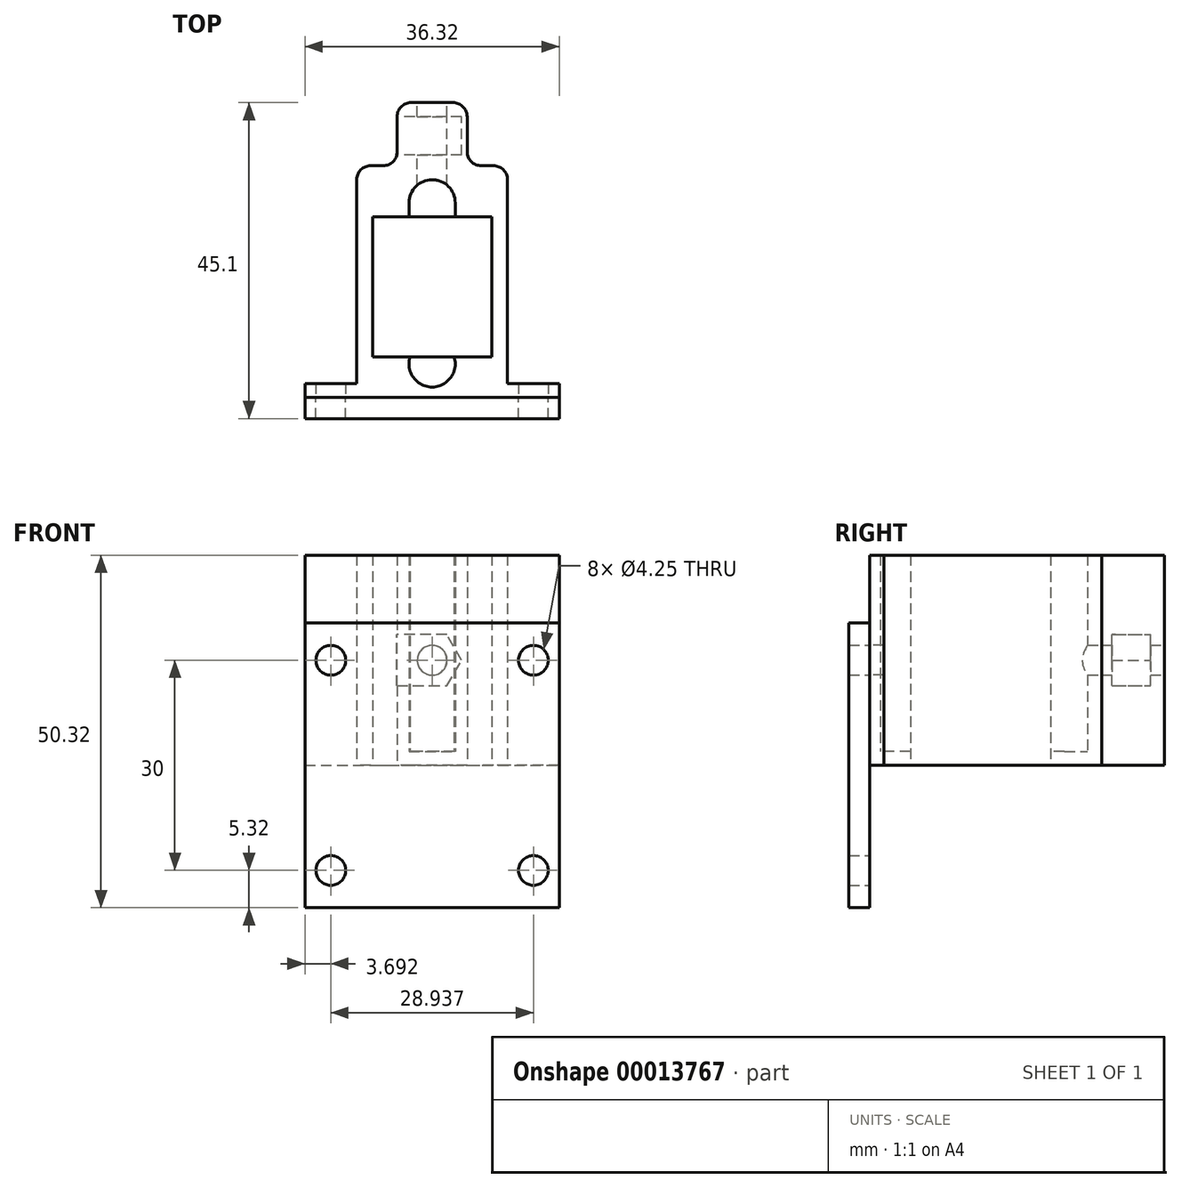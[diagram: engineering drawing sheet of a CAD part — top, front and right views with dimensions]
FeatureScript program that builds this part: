
annotation { "Feature Type Name" : "Feature", "Feature Type Description" : "" }
export const myFeature = defineFeature(function(context is Context, id is Id, definition is map)
    precondition{}
    {
        {
            var Q0;
            Q0=qCreatedBy(makeId("Top.planeOp"),FACE);
            var sketch = newSketch(context, id + "F0", { "sketchPlane" : qUnion([Q0])});
            skLineSegment(sketch, "E0.rect.bottom", {"start": v(8.5, -10) * mm, "end": v(-8.5, -10) * mm, "construction": true});
            skLineSegment(sketch, "E0.rect.top", {"start": v(8.5, 10) * mm, "end": v(-8.5, 10) * mm, "construction": true});
            skLineSegment(sketch, "E0.rect.left", {"start": v(8.5, -10) * mm, "end": v(8.5, 10) * mm, "construction": true});
            skLineSegment(sketch, "E0.rect.right", {"start": v(-8.5, -10) * mm, "end": v(-8.5, 10) * mm, "construction": true});
            skPoint(sketch, "E0.rect.middle", {"position": v(0, 0) * mm});
            skArc(sketch, "E1", {"start": v(3.3, 12) * mm, "mid": v(0, 15.3) * mm, "end": v(-3.3, 12) * mm});
            skArc(sketch, "E2", {"start": v(-3.14, -10) * mm, "mid": v(0, -14.3) * mm, "end": v(3.14, -10) * mm});
            skLineSegment(sketch, "E3", {"start": v(-3.3, 10) * mm, "end": v(-3.3, 12) * mm});
            skLineSegment(sketch, "E4", {"start": v(3.3, 10) * mm, "end": v(3.3, 12) * mm});
            skLineSegment(sketch, "E5", {"start": v(-3.3, 10) * mm, "end": v(-8.5, 10) * mm});
            skLineSegment(sketch, "E6", {"start": v(-8.5, -10) * mm, "end": v(-3.14, -10) * mm});
            skLineSegment(sketch, "E7", {"start": v(-8.5, 10) * mm, "end": v(-8.5, -10) * mm});
            skLineSegment(sketch, "E8.0.MirrorCS", {"start": v(3.3, 10) * mm, "end": v(8.5, 10) * mm});
            skLineSegment(sketch, "E9.0.MirrorCS", {"start": v(8.5, 10) * mm, "end": v(8.5, -10) * mm});
            skLineSegment(sketch, "E10.0.MirrorCS", {"start": v(8.5, -10) * mm, "end": v(3.14, -10) * mm});
            skPoint(sketch, "E11.center.orphan", {"position": v(0, 10) * mm});
            skLineSegment(sketch, "E12", {"start": v(0, -15.8) * mm, "end": v(-10.77, -15.8) * mm});
            skLineSegment(sketch, "E13", {"start": v(-10.77, -15.8) * mm, "end": v(-10.77, 17.3) * mm});
            skLineSegment(sketch, "E14", {"start": v(-10.77, 17.3) * mm, "end": v(-5, 17.3) * mm});
            skLineSegment(sketch, "E15.0.MirrorCS", {"start": v(10.77, 17.3) * mm, "end": v(5, 17.3) * mm});
            skLineSegment(sketch, "E16.0.MirrorCS", {"start": v(10.77, -15.8) * mm, "end": v(10.77, 17.3) * mm});
            skLineSegment(sketch, "E17.0.MirrorCS", {"start": v(0, -15.8) * mm, "end": v(10.77, -15.8) * mm});
            skLineSegment(sketch, "E18", {"start": v(-5, 17.3) * mm, "end": v(-5, 26.3) * mm});
            skLineSegment(sketch, "E19", {"start": v(-5, 26.3) * mm, "end": v(0, 26.3) * mm});
            skLineSegment(sketch, "E20.0.MirrorCS", {"start": v(5, 17.3) * mm, "end": v(5, 26.3) * mm});
            skLineSegment(sketch, "E21.0.MirrorCS", {"start": v(5, 26.3) * mm, "end": v(0, 26.3) * mm});
            skPoint(sketch, "E22.orphan", {"position": v(0, 17.3) * mm});
            skSolve(sketch);
        }
        {
            var Q0;
            Q0 = qSketchRegion(id + "F0", true);
            var Q1;
            Q1=makeQuery(id+"F0.imprint","IMPRINT",FACE,{"disambiguationData":[TD([[makeQuery(id+"F0.imprint","IMPRINT",EDGE,{"derivedFrom":sQuery(id+"F0.wireOp",EDGE,"E1")}),1.0]])]});
            extrude(context, id + "F1", {"entities" : qUnion([Q0, Q1]), "depth" : 2 * mm});
        }
        {
            var Q0;
            Q0 = qSketchRegion(id + "F0", true);
            extrude(context, id + "F2", {"entities" : qUnion([Q0]), "operationType" : NewBodyOperationType.ADD, "depth" : 30 * mm});
        }
        {
            var Q0;
            Q0=makeQuery(id+"F1.opExtrude","CAP_FACE",FACE,{"disambiguationData":[OSD([sQuery(id+"F0.wireOp",EDGE,"E12"),sQuery(id+"F0.wireOp",EDGE,"E13"),sQuery(id+"F0.wireOp",EDGE,"E14"),sQuery(id+"F0.wireOp",EDGE,"E15.0.MirrorCS"),sQuery(id+"F0.wireOp",EDGE,"E16.0.MirrorCS"),sQuery(id+"F0.wireOp",EDGE,"E17.0.MirrorCS"),sQuery(id+"F0.wireOp",EDGE,"E18"),sQuery(id+"F0.wireOp",EDGE,"E19"),sQuery(id+"F0.wireOp",EDGE,"E20.0.MirrorCS"),sQuery(id+"F0.wireOp",EDGE,"E21.0.MirrorCS")])],"isStart":false});
            var sketch = newSketch(context, id + "F3", { "sketchPlane" : qUnion([Q0])});
            skLineSegment(sketch, "E23", {"start": v(-8.5, 10) * mm, "end": v(8.5, 10) * mm});
            skLineSegment(sketch, "E24", {"start": v(8.5, 10) * mm, "end": v(8.5, -10) * mm});
            skLineSegment(sketch, "E25", {"start": v(8.5, -10) * mm, "end": v(-8.5, -10) * mm});
            skLineSegment(sketch, "E26", {"start": v(-8.5, -10) * mm, "end": v(-8.5, 10) * mm});
            skSolve(sketch);
        }
        {
            var Q0;
            Q0 = qSketchRegion(id + "F3", true);
            extrude(context, id + "F4", {"entities" : qUnion([Q0]), "operationType" : NewBodyOperationType.REMOVE, "endBound" : BoundingType.THROUGH_ALL, "oppositeDirection" : true, "depth" : 25 * mm});
        }
        {
            var Q0;
            {var subQ0=sQuery(id+"F0.wireOp",EDGE,"E12");var subQ1=sQuery(id+"F0.wireOp",EDGE,"E17.0.MirrorCS");Q0=makeQuery(id+"F2.boolean.opBoolean","MERGE",FACE,{"derivedFrom":[makeQuery(id+"F1.opExtrude","SWEPT_FACE",FACE,{"disambiguationData":[OSD([subQ0,subQ1])]}),makeQuery(id+"F2.opExtrude","SWEPT_FACE",FACE,{"disambiguationData":[OSD([subQ0,subQ1])]})]});}
            var sketch = newSketch(context, id + "F5", { "sketchPlane" : qUnion([Q0])});
            skLineSegment(sketch, "E27", {"start": v(-10.77, 30) * mm, "end": v(-18.16, 30) * mm});
            skLineSegment(sketch, "E28", {"start": v(-18.16, 30) * mm, "end": v(-18.16, 0) * mm});
            skLineSegment(sketch, "E29", {"start": v(-18.16, 0) * mm, "end": v(-10.77, 0) * mm});
            skLineSegment(sketch, "E30.0.MirrorCS", {"start": v(10.77, 30) * mm, "end": v(18.16, 30) * mm});
            skLineSegment(sketch, "E31.0.MirrorCS", {"start": v(18.16, 30) * mm, "end": v(18.16, 0) * mm});
            skLineSegment(sketch, "E32.0.MirrorCS", {"start": v(18.16, 0) * mm, "end": v(10.77, 0) * mm});
            skLineSegment(sketch, "E33", {"start": v(-14.47, 30) * mm, "end": v(-14.47, 0) * mm, "construction": true});
            skCircle(sketch, "E34", {"center": v(-14.47, 15) * mm, "radius": 2.12 * mm});
            skCircle(sketch, "E35.0.MirrorC", {"center": v(14.47, 15) * mm, "radius": 2.12 * mm});
            skLineSegment(sketch, "E36", {"start": v(-10.77, 30) * mm, "end": v(-10.77, 0) * mm});
            skLineSegment(sketch, "E37.0.MirrorCS", {"start": v(10.77, 30) * mm, "end": v(10.77, 0) * mm});
            skSolve(sketch);
        }
        {
            var Q0;
            Q0 = qSketchRegion(id + "F5", true);
            extrude(context, id + "F6", {"entities" : qUnion([Q0]), "operationType" : NewBodyOperationType.ADD, "oppositeDirection" : true, "depth" : 2 * mm});
        }
        {
            var Q0;
            {var subQ0=sQuery(id+"F0.wireOp",EDGE,"E19");var subQ1=sQuery(id+"F0.wireOp",EDGE,"E21.0.MirrorCS");Q0=makeQuery(id+"F2.boolean.opBoolean","MERGE",FACE,{"derivedFrom":[makeQuery(id+"F1.opExtrude","SWEPT_FACE",FACE,{"disambiguationData":[OSD([subQ0,subQ1])]}),makeQuery(id+"F2.opExtrude","SWEPT_FACE",FACE,{"disambiguationData":[OSD([subQ0,subQ1])]})]});}
            var sketch = newSketch(context, id + "F7", { "sketchPlane" : qUnion([Q0])});
            skLineSegment(sketch, "E38", {"start": v(0, 30) * mm, "end": v(0, 0) * mm, "construction": true});
            skCircle(sketch, "E39.cCircle", {"center": v(0, 15) * mm, "radius": 3.65 * mm, "construction": true});
            skLineSegment(sketch, "E39.0", {"start": v(2.1, 11.35) * mm, "end": v(-2.1, 11.35) * mm});
            skLineSegment(sketch, "E39.1", {"start": v(-2.1, 11.35) * mm, "end": v(-4.21, 15) * mm});
            skLineSegment(sketch, "E39.2", {"start": v(-4.21, 15) * mm, "end": v(-2.1, 18.65) * mm});
            skLineSegment(sketch, "E39.3", {"start": v(-2.1, 18.65) * mm, "end": v(2.1, 18.65) * mm});
            skPoint(sketch, "E39.0.midPoint", {"position": v(0, 11.35) * mm});
            skLineSegment(sketch, "E40", {"start": v(2.1, 18.65) * mm, "end": v(5, 18.65) * mm});
            skLineSegment(sketch, "E41", {"start": v(2.1, 11.35) * mm, "end": v(5, 11.35) * mm});
            skLineSegment(sketch, "E42", {"start": v(5, 11.35) * mm, "end": v(5, 18.65) * mm});
            skPoint(sketch, "E43.orphan", {"position": v(4.21, 15) * mm});
            skSolve(sketch);
        }
        {
            var Q0;
            Q0 = qSketchRegion(id + "F7", true);
            extrude(context, id + "F8", {"entities" : qUnion([Q0]), "operationType" : NewBodyOperationType.REMOVE, "oppositeDirection" : true, "depth" : 7.5 * mm});
        }
        {
            var Q0;
            {var subQ0=sQuery(id+"F0.wireOp",EDGE,"E19");var subQ1=sQuery(id+"F0.wireOp",EDGE,"E21.0.MirrorCS");Q0=makeQuery(id+"F2.boolean.opBoolean","MERGE",FACE,{"derivedFrom":[makeQuery(id+"F1.opExtrude","SWEPT_FACE",FACE,{"disambiguationData":[OSD([subQ0,subQ1])]}),makeQuery(id+"F2.opExtrude","SWEPT_FACE",FACE,{"disambiguationData":[OSD([subQ0,subQ1])]})]});}
            var sketch = newSketch(context, id + "F9", { "sketchPlane" : qUnion([Q0])});
            skLineSegment(sketch, "E44", {"start": v(5, 18.65) * mm, "end": v(-2.1, 18.65) * mm});
            skLineSegment(sketch, "E45", {"start": v(-2.1, 18.65) * mm, "end": v(-4.21, 15) * mm});
            skLineSegment(sketch, "E46", {"start": v(-4.21, 15) * mm, "end": v(-2.1, 11.35) * mm});
            skLineSegment(sketch, "E47", {"start": v(-2.1, 11.35) * mm, "end": v(5, 11.35) * mm});
            skLineSegment(sketch, "E48", {"start": v(5, 11.35) * mm, "end": v(5, 18.65) * mm});
            skLineSegment(sketch, "E49", {"start": v(0, 30) * mm, "end": v(0, 0) * mm, "construction": true});
            skSolve(sketch);
        }
        {
            var Q0;
            Q0 = qSketchRegion(id + "F9", true);
            extrude(context, id + "F10", {"entities" : qUnion([Q0]), "operationType" : NewBodyOperationType.ADD, "oppositeDirection" : true, "depth" : 2 * mm});
        }
        {
            var Q0;
            {var subQ0=sQuery(id+"F0.wireOp",EDGE,"E15.0.MirrorCS");var subQ1=sQuery(id+"F0.wireOp",EDGE,"E16.0.MirrorCS");Q0=makeQuery(id+"F2.boolean.opBoolean","MERGE",EDGE,{"derivedFrom":[makeQuery(id+"F1.opExtrude","SWEPT_EDGE",EDGE,{"disambiguationData":[OSD([subQ0,subQ1])]}),makeQuery(id+"F2.opExtrude","SWEPT_EDGE",EDGE,{"disambiguationData":[OSD([subQ0,subQ1])]})]});}
            var Q1;
            {var subQ0=sQuery(id+"F0.wireOp",EDGE,"E13");var subQ1=sQuery(id+"F0.wireOp",EDGE,"E14");Q1=makeQuery(id+"F2.boolean.opBoolean","MERGE",EDGE,{"derivedFrom":[makeQuery(id+"F1.opExtrude","SWEPT_EDGE",EDGE,{"disambiguationData":[OSD([subQ0,subQ1])]}),makeQuery(id+"F2.opExtrude","SWEPT_EDGE",EDGE,{"disambiguationData":[OSD([subQ0,subQ1])]})]});}
            var Q2;
            {var subQ0=sQuery(id+"F0.wireOp",EDGE,"E20.0.MirrorCS");var subQ1=sQuery(id+"F0.wireOp",EDGE,"E21.0.MirrorCS");Q2=makeQuery(id+"F2.boolean.opBoolean","MERGE",EDGE,{"derivedFrom":[makeQuery(id+"F1.opExtrude","SWEPT_EDGE",EDGE,{"disambiguationData":[OSD([subQ0,subQ1])]}),makeQuery(id+"F2.opExtrude","SWEPT_EDGE",EDGE,{"disambiguationData":[OSD([subQ0,subQ1])]})]});}
            var Q3;
            {var subQ0=sQuery(id+"F0.wireOp",EDGE,"E15.0.MirrorCS");var subQ1=sQuery(id+"F0.wireOp",EDGE,"E20.0.MirrorCS");Q3=makeQuery(id+"F2.boolean.opBoolean","MERGE",EDGE,{"derivedFrom":[makeQuery(id+"F1.opExtrude","SWEPT_EDGE",EDGE,{"disambiguationData":[OSD([subQ0,subQ1])]}),makeQuery(id+"F2.opExtrude","SWEPT_EDGE",EDGE,{"disambiguationData":[OSD([subQ0,subQ1])]})]});}
            var Q4;
            {var subQ0=sQuery(id+"F0.wireOp",EDGE,"E18");var subQ1=sQuery(id+"F0.wireOp",EDGE,"E19");var subQ2=makeQuery(id+"F2.boolean.opBoolean","MERGE",EDGE,{"derivedFrom":[makeQuery(id+"F1.opExtrude","SWEPT_EDGE",EDGE,{"disambiguationData":[OSD([subQ0,subQ1])]}),makeQuery(id+"F2.opExtrude","SWEPT_EDGE",EDGE,{"disambiguationData":[OSD([subQ0,subQ1])]})]});Q4=makeQuery(id+"F10.boolean.opBoolean","MERGE",EDGE,{"derivedFrom":[makeQuery(id+"F8.boolean.opBoolean","SPLIT",EDGE,{"disambiguationData":[TD([makeQuery(id+"F6.opExtrude","SWEPT_FACE",FACE,{"disambiguationData":[OSD([sQuery(id+"F5.wireOp",EDGE,"E29")])]})])],"derivedFrom":subQ2}),makeQuery(id+"F8.boolean.opBoolean","SPLIT",EDGE,{"disambiguationData":[TD([makeQuery(id+"F6.opExtrude","SWEPT_FACE",FACE,{"disambiguationData":[OSD([sQuery(id+"F5.wireOp",EDGE,"E27")])]})])],"derivedFrom":subQ2}),makeQuery(id+"F10.opExtrude","CAP_EDGE",EDGE,{"disambiguationData":[OSD([sQuery(id+"F9.wireOp",EDGE,"E48")])],"isStart":true})]});}
            var Q5;
            {var subQ0=sQuery(id+"F0.wireOp",EDGE,"E14");var subQ1=sQuery(id+"F0.wireOp",EDGE,"E18");Q5=makeQuery(id+"F8.boolean.opBoolean","SPLIT",EDGE,{"disambiguationData":[TD([makeQuery(id+"F6.opExtrude","SWEPT_FACE",FACE,{"disambiguationData":[OSD([sQuery(id+"F5.wireOp",EDGE,"E29")])]})])],"derivedFrom":makeQuery(id+"F2.boolean.opBoolean","MERGE",EDGE,{"derivedFrom":[makeQuery(id+"F1.opExtrude","SWEPT_EDGE",EDGE,{"disambiguationData":[OSD([subQ0,subQ1])]}),makeQuery(id+"F2.opExtrude","SWEPT_EDGE",EDGE,{"disambiguationData":[OSD([subQ0,subQ1])]})]})});}
            var Q6;
            {var subQ0=sQuery(id+"F0.wireOp",EDGE,"E14");var subQ1=sQuery(id+"F0.wireOp",EDGE,"E18");Q6=makeQuery(id+"F8.boolean.opBoolean","SPLIT",EDGE,{"disambiguationData":[TD([makeQuery(id+"F6.opExtrude","SWEPT_FACE",FACE,{"disambiguationData":[OSD([sQuery(id+"F5.wireOp",EDGE,"E27")])]})])],"derivedFrom":makeQuery(id+"F2.boolean.opBoolean","MERGE",EDGE,{"derivedFrom":[makeQuery(id+"F1.opExtrude","SWEPT_EDGE",EDGE,{"disambiguationData":[OSD([subQ0,subQ1])]}),makeQuery(id+"F2.opExtrude","SWEPT_EDGE",EDGE,{"disambiguationData":[OSD([subQ0,subQ1])]})]})});}
            fillet(context, id + "F11", {"entities" : qUnion([Q0, Q1, Q2, Q3, Q4, Q5, Q6]), "radius" : 2 * mm, "tangentPropagation" : true, "allowEdgeOverflow" : false});
        }
        {
            var Q0;
            {var subQ0=sQuery(id+"F0.wireOp",EDGE,"E19");var subQ1=sQuery(id+"F0.wireOp",EDGE,"E21.0.MirrorCS");Q0=makeQuery(id+"F10.boolean.opBoolean","MERGE",FACE,{"derivedFrom":[makeQuery(id+"F2.boolean.opBoolean","MERGE",FACE,{"derivedFrom":[makeQuery(id+"F1.opExtrude","SWEPT_FACE",FACE,{"disambiguationData":[OSD([subQ0,subQ1])]}),makeQuery(id+"F2.opExtrude","SWEPT_FACE",FACE,{"disambiguationData":[OSD([subQ0,subQ1])]})]}),makeQuery(id+"F10.opExtrude","CAP_FACE",FACE,{"disambiguationData":[OSD([sQuery(id+"F9.wireOp",EDGE,"E44"),sQuery(id+"F9.wireOp",EDGE,"E45"),sQuery(id+"F9.wireOp",EDGE,"E46"),sQuery(id+"F9.wireOp",EDGE,"E47"),sQuery(id+"F9.wireOp",EDGE,"E48")])],"isStart":true})]});}
            var sketch = newSketch(context, id + "F12", { "sketchPlane" : qUnion([Q0])});
            skLineSegment(sketch, "E50", {"start": v(0, 30) * mm, "end": v(0, 0) * mm, "construction": true});
            skCircle(sketch, "E51", {"center": v(0, 15) * mm, "radius": 2.12 * mm});
            skSolve(sketch);
        }
        {
            var Q0;
            Q0 = qSketchRegion(id + "F12", true);
            extrude(context, id + "F13", {"entities" : qUnion([Q0]), "operationType" : NewBodyOperationType.REMOVE, "oppositeDirection" : true, "depth" : 25 * mm});
        }
        {
            var Q0;
            {var subQ0=sQuery(id+"F0.wireOp",EDGE,"E12");var subQ1=sQuery(id+"F0.wireOp",EDGE,"E17.0.MirrorCS");Q0=makeQuery(id+"F6.boolean.opBoolean","MERGE",FACE,{"derivedFrom":[makeQuery(id+"F2.boolean.opBoolean","MERGE",FACE,{"derivedFrom":[makeQuery(id+"F1.opExtrude","SWEPT_FACE",FACE,{"disambiguationData":[OSD([subQ0,subQ1])]}),makeQuery(id+"F2.opExtrude","SWEPT_FACE",FACE,{"disambiguationData":[OSD([subQ0,subQ1])]})]}),makeQuery(id+"F6.opExtrude","CAP_FACE",FACE,{"disambiguationData":[OSD([sQuery(id+"F5.wireOp",EDGE,"E27"),sQuery(id+"F5.wireOp",EDGE,"E28"),sQuery(id+"F5.wireOp",EDGE,"E29"),sQuery(id+"F5.wireOp",EDGE,"E34"),sQuery(id+"F5.wireOp",EDGE,"E36")])],"isStart":true}),makeQuery(id+"F6.opExtrude","CAP_FACE",FACE,{"disambiguationData":[OSD([sQuery(id+"F5.wireOp",EDGE,"E30.0.MirrorCS"),sQuery(id+"F5.wireOp",EDGE,"E31.0.MirrorCS"),sQuery(id+"F5.wireOp",EDGE,"E32.0.MirrorCS"),sQuery(id+"F5.wireOp",EDGE,"E35.0.MirrorC"),sQuery(id+"F5.wireOp",EDGE,"E37.0.MirrorCS")])],"isStart":true})]});}
            var sketch = newSketch(context, id + "F14", { "sketchPlane" : qUnion([Q0])});
            skLineSegment(sketch, "E52", {"start": v(-18.16, 0) * mm, "end": v(-18.16, 20.32) * mm});
            skLineSegment(sketch, "E53", {"start": v(-18.16, 20.32) * mm, "end": v(18.16, 20.32) * mm});
            skLineSegment(sketch, "E54", {"start": v(18.16, 20.32) * mm, "end": v(18.16, 0) * mm});
            skLineSegment(sketch, "E55.0.MirrorCS", {"start": v(-18.16, -20.32) * mm, "end": v(18.16, -20.32) * mm});
            skLineSegment(sketch, "E56.0.MirrorCS", {"start": v(-18.16, 0) * mm, "end": v(-18.16, -20.32) * mm});
            skLineSegment(sketch, "E57.0.MirrorCS", {"start": v(18.16, -20.32) * mm, "end": v(18.16, 0) * mm});
            skCircle(sketch, "E58", {"center": v(-14.47, 15) * mm, "radius": 2.12 * mm});
            skCircle(sketch, "E59", {"center": v(14.47, 15) * mm, "radius": 2.12 * mm});
            skCircle(sketch, "E60.0.MirrorC", {"center": v(-14.47, -15) * mm, "radius": 2.12 * mm});
            skCircle(sketch, "E61.0.MirrorC", {"center": v(14.47, -15) * mm, "radius": 2.12 * mm});
            skSolve(sketch);
        }
        {
            var Q0;
            Q0 = qSketchRegion(id + "F14", true);
            extrude(context, id + "F15", {"entities" : qUnion([Q0]), "depth" : 3 * mm});
        }
    });
